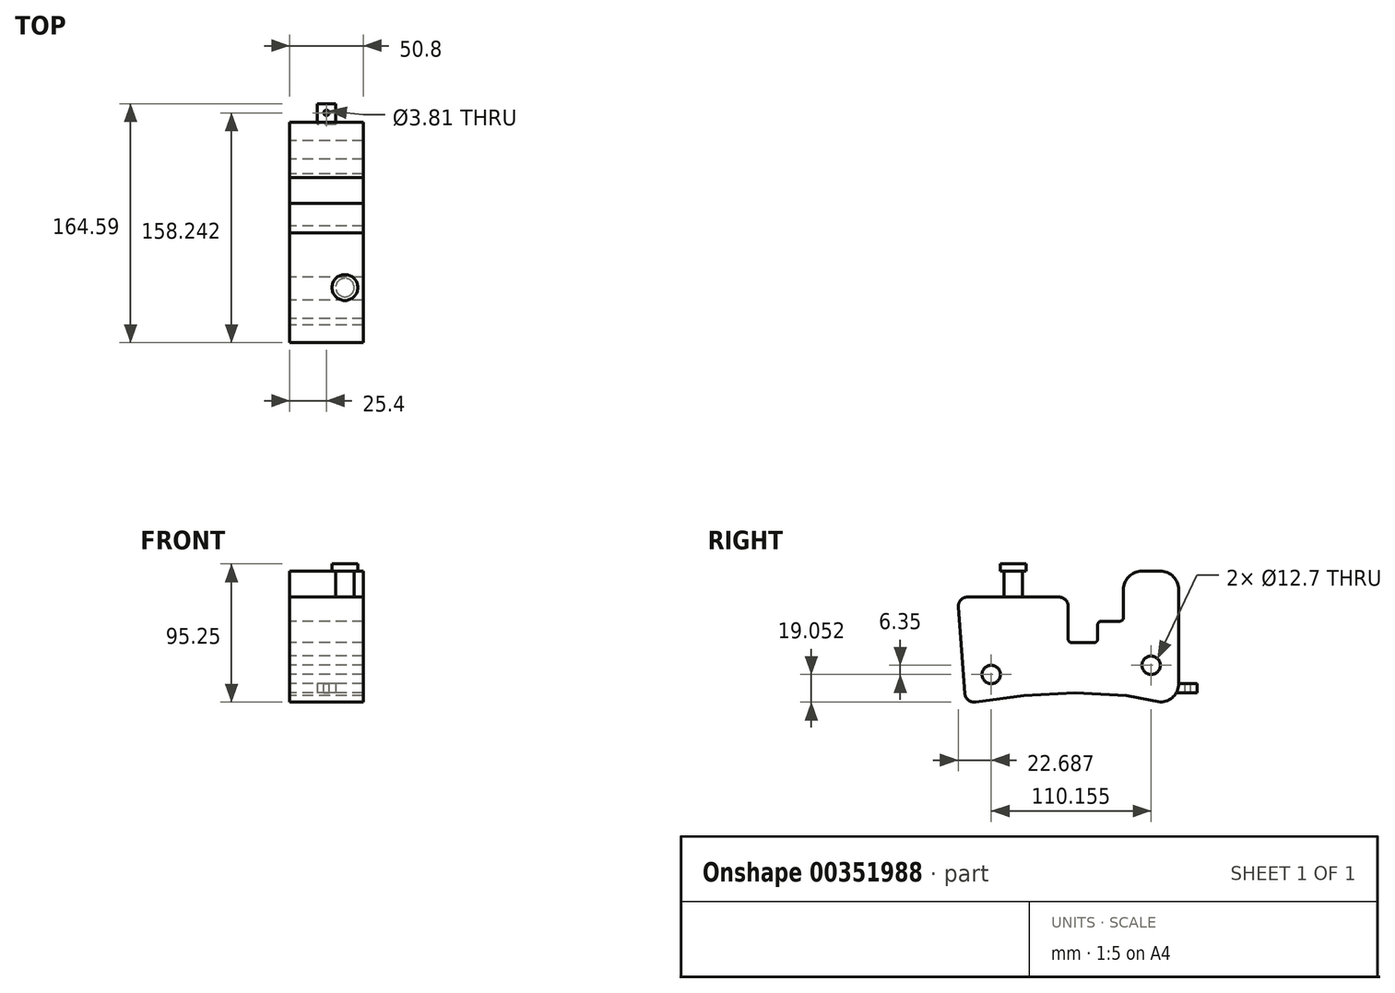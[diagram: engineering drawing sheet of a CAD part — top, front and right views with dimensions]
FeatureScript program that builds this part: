
annotation { "Feature Type Name" : "Feature", "Feature Type Description" : "" }
export const myFeature = defineFeature(function(context is Context, id is Id, definition is map)
    precondition{}
    {
        {
            var Q0;
            Q0=qCreatedBy(makeId("Right.planeOp"),FACE);
            var sketch = newSketch(context, id + "F0", { "sketchPlane" : qUnion([Q0])});
            skLineSegment(sketch, "E0.bottom", {"start": v(-20.13, 34.98) * mm, "end": v(-7.43, 34.98) * mm});
            skLineSegment(sketch, "E0.top", {"start": v(-134.43, -55.19) * mm, "end": v(-7.43, -55.19) * mm});
            skLineSegment(sketch, "E0.right", {"start": v(5.27, 22.28) * mm, "end": v(5.27, -42.49) * mm});
            skLineSegment(sketch, "E1", {"start": v(-32.83, 22.28) * mm, "end": v(-32.83, 3.09) * mm});
            skLineSegment(sketch, "E2", {"start": v(-35.37, 0.55) * mm, "end": v(-48.07, 0.55) * mm});
            skLineSegment(sketch, "E3", {"start": v(-50.6, -2) * mm, "end": v(-50.6, -11.73) * mm});
            skLineSegment(sketch, "E4", {"start": v(-53.15, -14.27) * mm, "end": v(-68.39, -14.27) * mm});
            skLineSegment(sketch, "E5", {"start": v(-70.93, -11.73) * mm, "end": v(-70.93, 10.85) * mm});
            skLineSegment(sketch, "E6", {"start": v(-77.28, 17.2) * mm, "end": v(-139.5, 17.2) * mm});
            skPoint(sketch, "E7.newPointA", {"position": v(-147.13, 17.2) * mm});
            skPoint(sketch, "E7.newPointB", {"position": v(-147.13, 33.71) * mm});
            skPoint(sketch, "E8.visualSharp", {"position": v(-70.93, 17.2) * mm});
            skArc(sketch, "E8.filletArc", {"start": v(-70.93, 10.85) * mm, "mid": v(-72.79, 15.34) * mm, "end": v(-77.28, 17.2) * mm});
            skPoint(sketch, "E9.visualSharp", {"position": v(-70.93, -14.27) * mm});
            skArc(sketch, "E9.filletArc", {"start": v(-70.93, -11.73) * mm, "mid": v(-70.18, -13.52) * mm, "end": v(-68.39, -14.27) * mm});
            skPoint(sketch, "E10.visualSharp", {"position": v(-50.6, -14.27) * mm});
            skArc(sketch, "E10.filletArc", {"start": v(-53.15, -14.27) * mm, "mid": v(-51.35, -13.52) * mm, "end": v(-50.6, -11.73) * mm});
            skPoint(sketch, "E11.visualSharp", {"position": v(-50.6, 0.55) * mm});
            skArc(sketch, "E11.filletArc", {"start": v(-48.07, 0.55) * mm, "mid": v(-49.86, -0.2) * mm, "end": v(-50.6, -2) * mm});
            skPoint(sketch, "E12.visualSharp", {"position": v(-32.83, 0.55) * mm});
            skArc(sketch, "E12.filletArc", {"start": v(-35.37, 0.55) * mm, "mid": v(-33.57, 1.3) * mm, "end": v(-32.83, 3.09) * mm});
            skPoint(sketch, "E13.newPointA", {"position": v(-32.83, 34.98) * mm});
            skArc(sketch, "E13.filletArc", {"start": v(-20.13, 34.98) * mm, "mid": v(-29.1, 31.26) * mm, "end": v(-32.83, 22.28) * mm});
            skPoint(sketch, "E14.visualSharp", {"position": v(5.27, 34.98) * mm});
            skArc(sketch, "E14.filletArc", {"start": v(5.27, 22.28) * mm, "mid": v(1.55, 31.26) * mm, "end": v(-7.43, 34.98) * mm});
            skPoint(sketch, "E15.visualSharp", {"position": v(5.27, -55.19) * mm});
            skArc(sketch, "E15.filletArc", {"start": v(-7.43, -55.19) * mm, "mid": v(1.55, -51.47) * mm, "end": v(5.27, -42.49) * mm});
            skPoint(sketch, "E16.visualSharp", {"position": v(-147.13, -55.19) * mm});
            skLineSegment(sketch, "E17", {"start": v(-139.5, 17.2) * mm, "end": v(-140.27, 17.2) * mm});
            skLineSegment(sketch, "E18", {"start": v(-146.6, 10.37) * mm, "end": v(-142.03, -49.32) * mm});
            skLineSegment(sketch, "E19", {"start": v(-134.43, -55.19) * mm, "end": v(-135.7, -55.19) * mm});
            skArc(sketch, "E20.filletArc", {"start": v(-140.27, 17.2) * mm, "mid": v(-144.93, 15.17) * mm, "end": v(-146.6, 10.37) * mm});
            skPoint(sketch, "E21.visualSharp", {"position": v(-141.58, -55.19) * mm});
            skArc(sketch, "E21.filletArc", {"start": v(-142.03, -49.32) * mm, "mid": v(-140.01, -53.5) * mm, "end": v(-135.7, -55.19) * mm});
            skLineSegment(sketch, "E22", {"start": v(-134.43, -55.19) * mm, "end": v(-101.49, -50.83) * mm});
            skLineSegment(sketch, "E23", {"start": v(-101.49, -50.83) * mm, "end": v(-66.22, -48.62) * mm});
            skLineSegment(sketch, "E24", {"start": v(-66.22, -48.62) * mm, "end": v(-30.51, -50.83) * mm});
            skLineSegment(sketch, "E25", {"start": v(-30.51, -50.83) * mm, "end": v(-7.43, -55.19) * mm});
            skCircle(sketch, "E26", {"center": v(-123.93, -36.14) * mm, "radius": 6.35 * mm});
            skCircle(sketch, "E27", {"center": v(-13.78, -29.79) * mm, "radius": 6.35 * mm});
            skSolve(sketch);
        }
        {
            var Q0;
            Q0=makeQuery(id+"F0.imprint","IMPRINT",FACE,{"disambiguationData":[TD([[makeQuery(id+"F0.imprint","IMPRINT",EDGE,{"derivedFrom":sQuery(id+"F0.wireOp",EDGE,"E0.bottom")}),-1.0]])]});
            extrude(context, id + "F1", {"entities" : qUnion([Q0]), "depth" : 50.8 * mm});
        }
        {
            var Q0;
            Q0=makeQuery(id+"F1.opExtrude","SWEPT_FACE",FACE,{"disambiguationData":[OSD([sQuery(id+"F0.wireOp",EDGE,"E6"),sQuery(id+"F0.wireOp",EDGE,"E17")])]});
            var sketch = newSketch(context, id + "F2", { "sketchPlane" : qUnion([Q0])});
            skCircle(sketch, "E28", {"center": v(38.1, -108.77) * mm, "radius": 6.35 * mm});
            skSolve(sketch);
        }
        {
            var Q0;
            Q0=makeQuery(id+"F2.imprint","IMPRINT",FACE,{"disambiguationData":[TD([[makeQuery(id+"F2.imprint","IMPRINT",EDGE,{"derivedFrom":sQuery(id+"F2.wireOp",EDGE,"E28")}),1.0]])]});
            extrude(context, id + "F3", {"entities" : qUnion([Q0]), "operationType" : NewBodyOperationType.ADD, "depth" : 17.78 * mm});
        }
        {
            var Q0;
            Q0=makeQuery(id+"F3.opExtrude","CAP_FACE",FACE,{"disambiguationData":[OSD([sQuery(id+"F2.wireOp",EDGE,"E28")])],"isStart":false});
            var sketch = newSketch(context, id + "F4", { "sketchPlane" : qUnion([Q0])});
            skCircle(sketch, "E29", {"center": v(38.1, -108.77) * mm, "radius": 8.89 * mm});
            skSolve(sketch);
        }
        {
            var Q0;
            Q0=makeQuery(id+"F4.imprint","IMPRINT",FACE,{"disambiguationData":[TD([[makeQuery(id+"F4.imprint","IMPRINT",EDGE,{"derivedFrom":sQuery(id+"F4.wireOp",EDGE,"E29")}),1.0]])]});
            var Q1;
            Q1=makeQuery(id+"F4.imprint","IMPRINT",FACE,{"disambiguationData":[TD([[makeQuery(id+"F4.imprint","IMPRINT",EDGE,{"derivedFrom":makeQuery(id+"F3.opExtrude","CAP_EDGE",EDGE,{"disambiguationData":[OSD([sQuery(id+"F2.wireOp",EDGE,"E28")])],"isStart":false})}),1.0]])]});
            extrude(context, id + "F5", {"entities" : qUnion([Q0, Q1]), "operationType" : NewBodyOperationType.ADD, "depth" : 5.08 * mm});
        }
        {
            var Q0;
            Q0=makeQuery(id+"F1.opExtrude","SWEPT_FACE",FACE,{"disambiguationData":[OSD([sQuery(id+"F0.wireOp",EDGE,"E0.right")])]});
            var sketch = newSketch(context, id + "F6", { "sketchPlane" : qUnion([Q0])});
            skLineSegment(sketch, "E30.bottom", {"start": v(-31.75, -42.49) * mm, "end": v(-19.05, -42.49) * mm});
            skLineSegment(sketch, "E30.top", {"start": v(-31.75, -48.84) * mm, "end": v(-19.05, -48.84) * mm});
            skLineSegment(sketch, "E30.left", {"start": v(-31.75, -42.49) * mm, "end": v(-31.75, -48.84) * mm});
            skLineSegment(sketch, "E30.right", {"start": v(-19.05, -42.49) * mm, "end": v(-19.05, -48.84) * mm});
            skSolve(sketch);
        }
        {
            var Q0;
            Q0=makeQuery(id+"F6.imprint","IMPRINT",FACE,{"disambiguationData":[TD([[makeQuery(id+"F6.imprint","IMPRINT",EDGE,{"derivedFrom":sQuery(id+"F6.wireOp",EDGE,"E30.bottom")}),-1.0]])]});
            extrude(context, id + "F7", {"entities" : qUnion([Q0]), "operationType" : NewBodyOperationType.ADD, "depth" : 12.7 * mm, "hasSecondDirection" : true, "secondDirectionOppositeDirection" : true, "secondDirectionDepth" : 25.4 * mm});
        }
        {
            var Q0;
            Q0=makeQuery(id+"F7.opExtrude","SWEPT_FACE",FACE,{"disambiguationData":[OSD([sQuery(id+"F6.wireOp",EDGE,"E30.bottom")])]});
            var sketch = newSketch(context, id + "F8", { "sketchPlane" : qUnion([Q0])});
            skCircle(sketch, "E31", {"center": v(25.4, 11.62) * mm, "radius": 1.9 * mm});
            skPoint(sketch, "E31.centerSnap0", {"position": v(19.05, 11.62) * mm});
            skPoint(sketch, "E31.centerSnap1", {"position": v(25.4, 5.27) * mm});
            skSolve(sketch);
        }
        {
            var Q0;
            Q0=makeQuery(id+"F8.imprint","IMPRINT",FACE,{"disambiguationData":[TD([[makeQuery(id+"F8.imprint","IMPRINT",EDGE,{"derivedFrom":sQuery(id+"F8.wireOp",EDGE,"E31")}),1.0]])]});
            extrude(context, id + "F9", {"entities" : qUnion([Q0]), "operationType" : NewBodyOperationType.REMOVE, "oppositeDirection" : true, "depth" : 12.7 * mm});
        }
    });
